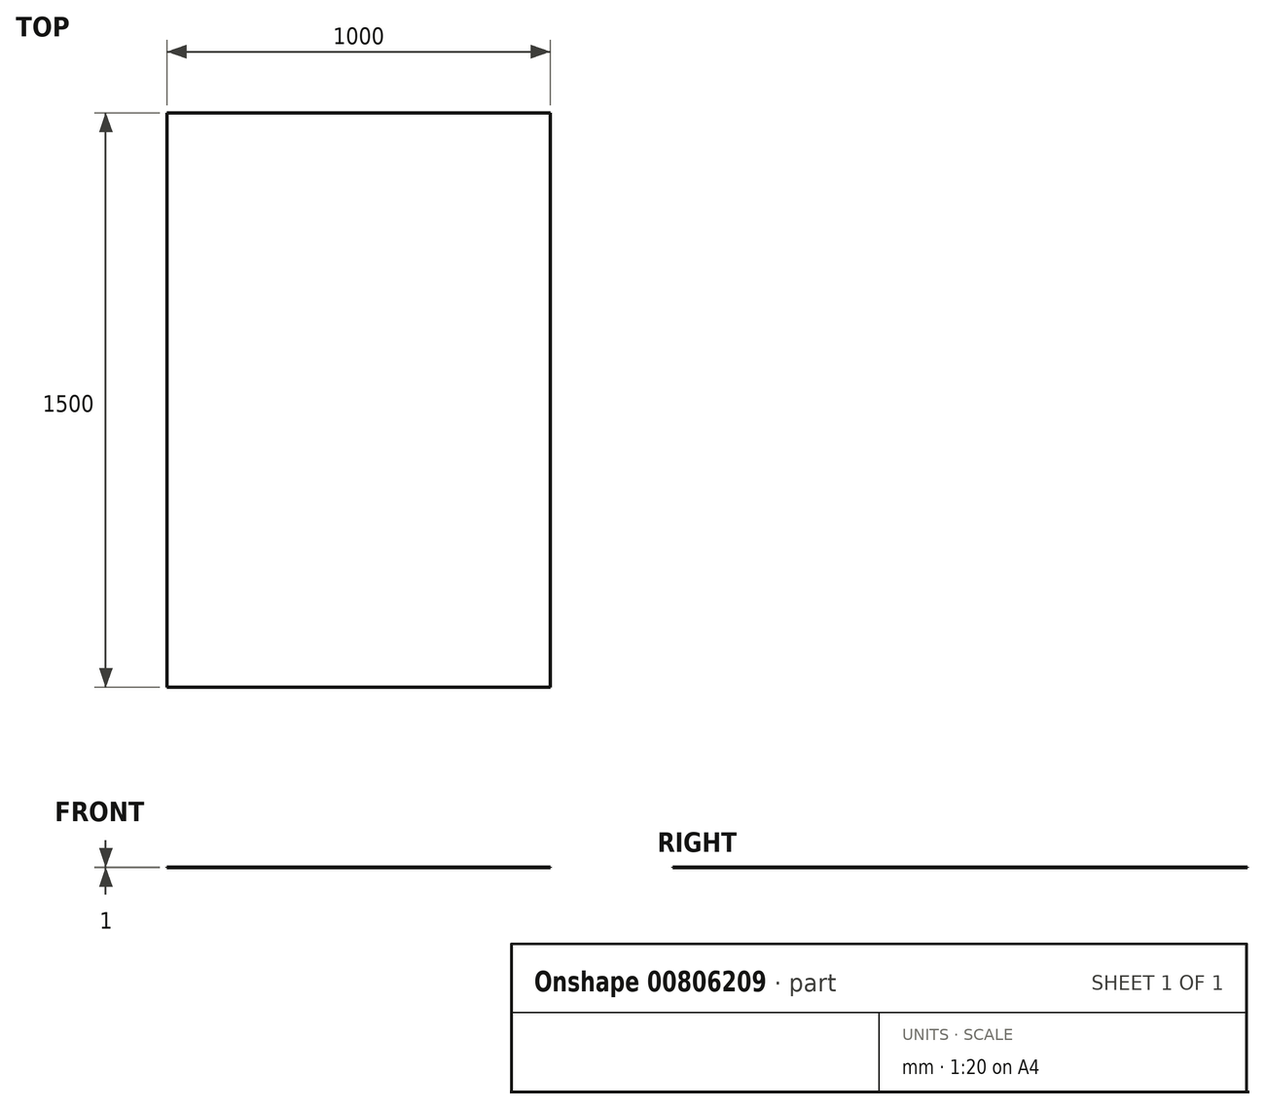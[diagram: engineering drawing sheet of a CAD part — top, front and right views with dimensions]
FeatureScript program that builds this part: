
annotation { "Feature Type Name" : "Feature", "Feature Type Description" : "" }
export const myFeature = defineFeature(function(context is Context, id is Id, definition is map)
    precondition{}
    {
        {
            var Q0;
            Q0=qCreatedBy(makeId("Top.planeOp"),FACE);
            var sketch = newSketch(context, id + "F0", { "sketchPlane" : qUnion([Q0])});
            skLineSegment(sketch, "E0.bottom", {"start": v(-497.47, 1249.41) * mm, "end": v(502.53, 1249.41) * mm});
            skLineSegment(sketch, "E0.top", {"start": v(-497.47, -250.59) * mm, "end": v(502.53, -250.59) * mm});
            skLineSegment(sketch, "E0.left", {"start": v(-497.47, 1249.41) * mm, "end": v(-497.47, -250.59) * mm});
            skLineSegment(sketch, "E0.right", {"start": v(502.53, 1249.41) * mm, "end": v(502.53, -250.59) * mm});
            skSolve(sketch);
        }
        {
            var Q0;
            Q0=makeQuery(id+"F0.imprint","IMPRINT",FACE,{"disambiguationData":[TD([[makeQuery(id+"F0.imprint","IMPRINT",EDGE,{"derivedFrom":sQuery(id+"F0.wireOp",EDGE,"E0.bottom")}),-1.0]])]});
            extrude(context, id + "F1", {"entities" : qUnion([Q0]), "depth" : 1 * mm, "offsetDistance" : 25 * mm});
        }
    });
